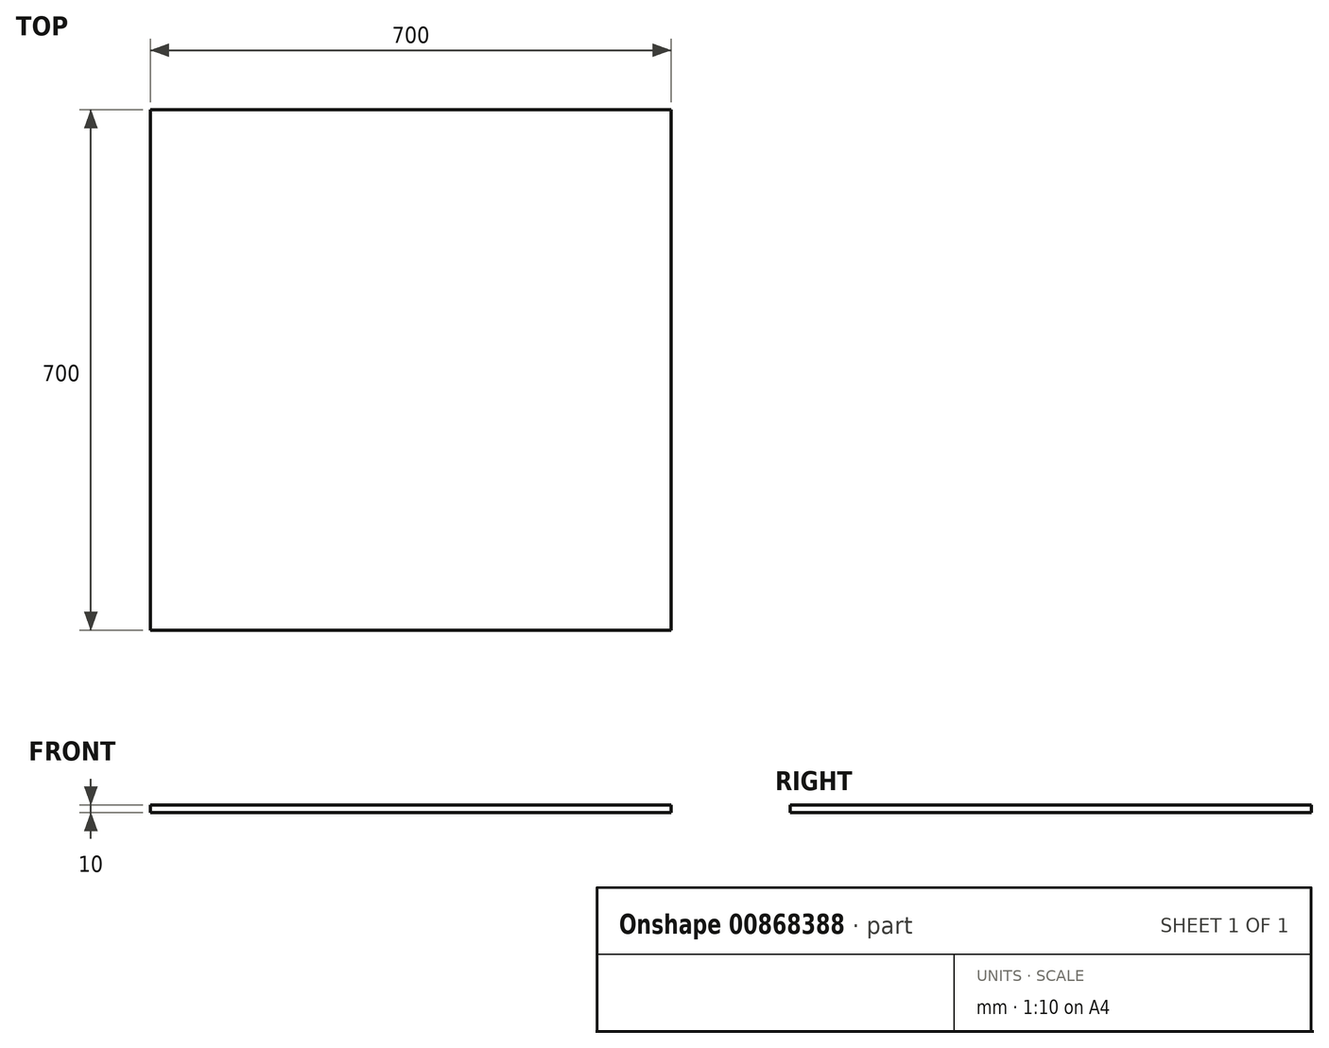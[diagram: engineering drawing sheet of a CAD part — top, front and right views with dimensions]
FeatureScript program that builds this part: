
annotation { "Feature Type Name" : "Feature", "Feature Type Description" : "" }
export const myFeature = defineFeature(function(context is Context, id is Id, definition is map)
    precondition{}
    {
        {
            var Q0;
            Q0=qCreatedBy(makeId("Top.planeOp"),FACE);
            var sketch = newSketch(context, id + "F0", { "sketchPlane" : qUnion([Q0])});
            skLineSegment(sketch, "E0.bottom", {"start": v(0, 0) * mm, "end": v(-700, 0) * mm});
            skLineSegment(sketch, "E0.top", {"start": v(0, 700) * mm, "end": v(-700, 700) * mm});
            skLineSegment(sketch, "E0.left", {"start": v(0, 0) * mm, "end": v(0, 700) * mm});
            skLineSegment(sketch, "E0.right", {"start": v(-700, 0) * mm, "end": v(-700, 700) * mm});
            skSolve(sketch);
        }
        {
            var Q0;
            Q0 = qSketchRegion(id + "F0", true);
            extrude(context, id + "F1", {"entities" : qUnion([Q0]), "depth" : 10 * mm, "offsetDistance" : 25 * mm});
        }
    });
